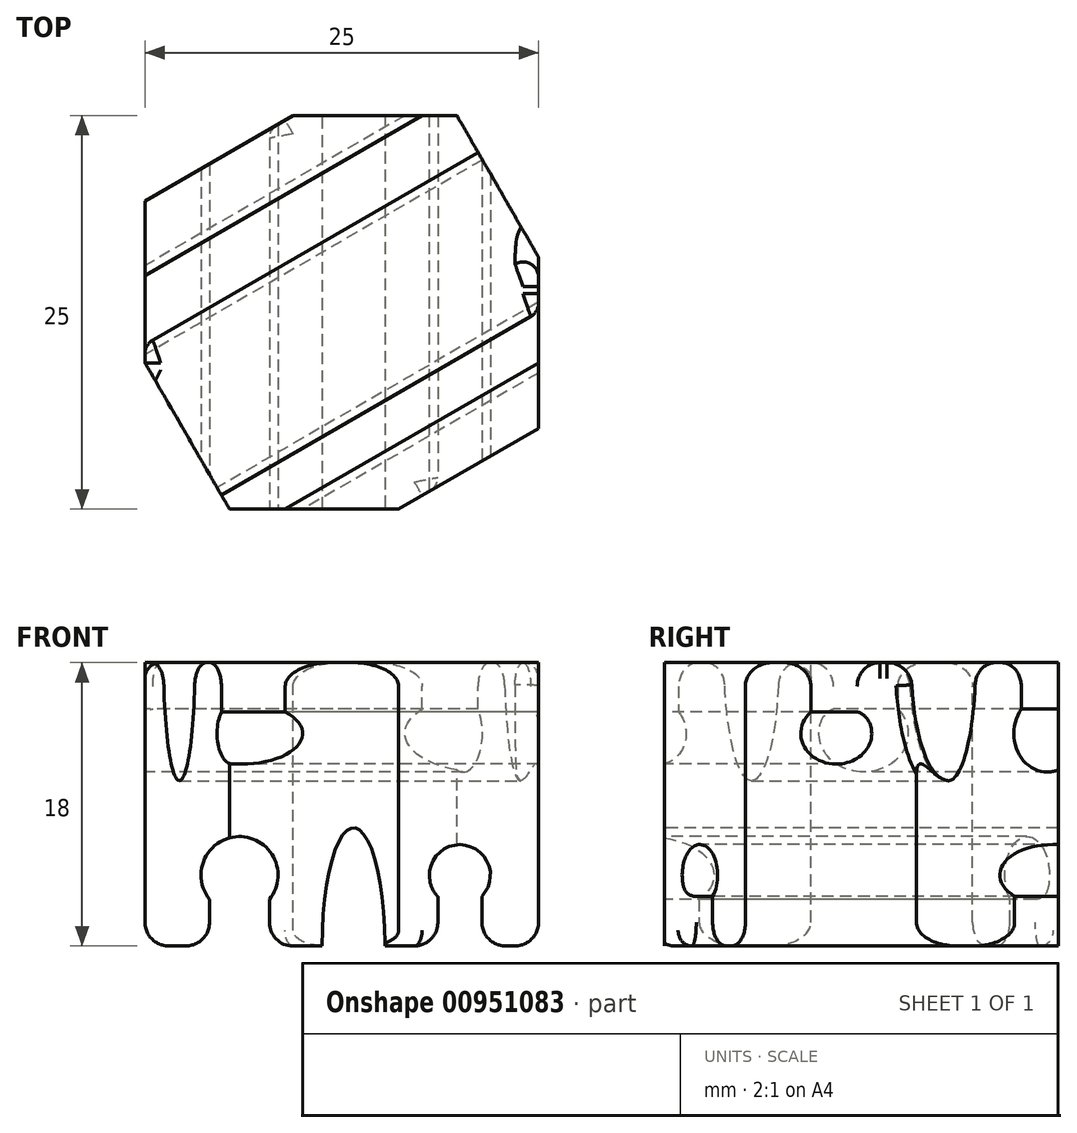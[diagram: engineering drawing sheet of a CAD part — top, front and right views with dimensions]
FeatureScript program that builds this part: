
annotation { "Feature Type Name" : "Feature", "Feature Type Description" : "" }
export const myFeature = defineFeature(function(context is Context, id is Id, definition is map)
    precondition{}
    {
        {
            var Q0;
            Q0=qCreatedBy(makeId("Top.planeOp"),FACE);
            var sketch = newSketch(context, id + "F0", { "sketchPlane" : qUnion([Q0])});
            skLineSegment(sketch, "E0.bottom", {"start": v(0, 0) * mm, "end": v(25, 0) * mm});
            skLineSegment(sketch, "E0.top", {"start": v(0, 25) * mm, "end": v(25, 25) * mm});
            skLineSegment(sketch, "E0.left", {"start": v(0, 0) * mm, "end": v(0, 25) * mm});
            skLineSegment(sketch, "E0.right", {"start": v(25, 0) * mm, "end": v(25, 25) * mm});
            skSolve(sketch);
        }
        {
            var Q0;
            Q0 = qSketchRegion(id + "F0", true);
            extrude(context, id + "F1", {"entities" : qUnion([Q0]), "depth" : 9 * mm, "offsetDistance" : 25 * mm});
        }
        {
            var Q0;
            Q0=makeQuery(id+"F1.opExtrude","SWEPT_FACE",FACE,{"disambiguationData":[OSD([sQuery(id+"F0.wireOp",EDGE,"E0.bottom")])]});
            var sketch = newSketch(context, id + "F2", { "sketchPlane" : qUnion([Q0])});
            skCircle(sketch, "E1", {"center": v(6, 4.5) * mm, "radius": 2.45 * mm});
            skPoint(sketch, "E1.centerSnap0", {"position": v(0, 4.5) * mm});
            skCircle(sketch, "E2", {"center": v(20, 4.5) * mm, "radius": 1.95 * mm});
            skEllipse(sketch, "E3", {"center": v(13.25, 0) * mm, "majorRadius": 7.5 * mm, "minorRadius": 2 * mm, "majorAxis": v(0, -1)});
            skSolve(sketch);
        }
        {
            var Q0;
            Q0 = qSketchRegion(id + "F2", true);
            var Q1;
            Q1=makeQuery(id+"F1.opExtrude","SWEPT_FACE",FACE,{"disambiguationData":[OSD([sQuery(id+"F0.wireOp",EDGE,"E0.top")])]});
            extrude(context, id + "F3", {"entities" : qUnion([Q0]), "operationType" : NewBodyOperationType.REMOVE, "endBound" : BoundingType.UP_TO_SURFACE, "oppositeDirection" : true, "depth" : 25 * mm, "endBoundEntityFace" : qUnion([Q1]), "offsetDistance" : 25 * mm});
        }
        {
            var Q0;
            Q0=makeQuery(id+"F1.opExtrude","CAP_FACE",FACE,{"disambiguationData":[OSD([sQuery(id+"F0.wireOp",EDGE,"E0.bottom"),sQuery(id+"F0.wireOp",EDGE,"E0.top"),sQuery(id+"F0.wireOp",EDGE,"E0.left"),sQuery(id+"F0.wireOp",EDGE,"E0.right")])],"isStart":false});
            var sketch = newSketch(context, id + "F4", { "sketchPlane" : qUnion([Q0])});
            skLineSegment(sketch, "E4", {"start": v(17.2, 29.5) * mm, "end": v(-4.44, 17) * mm});
            skLineSegment(sketch, "E5", {"start": v(-4.44, 17) * mm, "end": v(8.06, -4.65) * mm});
            skLineSegment(sketch, "E6", {"start": v(8.06, -4.65) * mm, "end": v(29.7, 7.85) * mm});
            skLineSegment(sketch, "E7", {"start": v(29.7, 7.85) * mm, "end": v(17.2, 29.5) * mm});
            skSolve(sketch);
        }
        {
            var Q0;
            Q0 = qSketchRegion(id + "F4", true);
            extrude(context, id + "F5", {"entities" : qUnion([Q0]), "operationType" : NewBodyOperationType.ADD, "depth" : 9 * mm, "offsetDistance" : 25 * mm});
        }
        {
            var Q0;
            Q0=makeQuery(id+"F5.opExtrude","SWEPT_FACE",FACE,{"disambiguationData":[OSD([sQuery(id+"F4.wireOp",EDGE,"E5")])]});
            var sketch = newSketch(context, id + "F6", { "sketchPlane" : qUnion([Q0])});
            skCircle(sketch, "E8", {"center": v(-10.94, 13.5) * mm, "radius": 2.45 * mm});
            skCircle(sketch, "E9", {"center": v(3.06, 13.5) * mm, "radius": 1.95 * mm});
            skEllipse(sketch, "E10", {"center": v(-3.7, 18) * mm, "majorRadius": 7.5 * mm, "minorRadius": 2 * mm, "majorAxis": v(0, -1)});
            skSolve(sketch);
        }
        {
            var Q0;
            Q0 = qSketchRegion(id + "F6", true);
            var Q1;
            Q1=makeQuery(id+"F5.opExtrude","SWEPT_FACE",FACE,{"disambiguationData":[OSD([sQuery(id+"F4.wireOp",EDGE,"E7")])]});
            extrude(context, id + "F7", {"entities" : qUnion([Q0]), "operationType" : NewBodyOperationType.REMOVE, "endBound" : BoundingType.UP_TO_SURFACE, "oppositeDirection" : true, "depth" : 25 * mm, "endBoundEntityFace" : qUnion([Q1]), "offsetDistance" : 25 * mm});
        }
        {
            var Q0;
            Q0=makeQuery(id+"F1.opExtrude","SWEPT_FACE",FACE,{"disambiguationData":[OSD([sQuery(id+"F0.wireOp",EDGE,"E0.bottom")])]});
            var sketch = newSketch(context, id + "F8", { "sketchPlane" : qUnion([Q0])});
            skLineSegment(sketch, "E11.bottom", {"start": v(4.1, 4.5) * mm, "end": v(7.9, 4.5) * mm});
            skLineSegment(sketch, "E11.top", {"start": v(4.1, -1) * mm, "end": v(7.9, -1) * mm});
            skLineSegment(sketch, "E11.left", {"start": v(4.1, 4.5) * mm, "end": v(4.1, -1) * mm});
            skLineSegment(sketch, "E11.right", {"start": v(7.9, 4.5) * mm, "end": v(7.9, -1) * mm});
            skLineSegment(sketch, "E12.bottom", {"start": v(18.6, 4.5) * mm, "end": v(21.4, 4.5) * mm});
            skLineSegment(sketch, "E12.top", {"start": v(18.6, -1) * mm, "end": v(21.4, -1) * mm});
            skLineSegment(sketch, "E12.left", {"start": v(18.6, 4.5) * mm, "end": v(18.6, -1) * mm});
            skLineSegment(sketch, "E12.right", {"start": v(21.4, 4.5) * mm, "end": v(21.4, -1) * mm});
            skSolve(sketch);
        }
        {
            var Q0;
            Q0 = qSketchRegion(id + "F8", true);
            var Q1;
            Q1=makeQuery(id+"F1.opExtrude","SWEPT_FACE",FACE,{"disambiguationData":[OSD([sQuery(id+"F0.wireOp",EDGE,"E0.top")])]});
            extrude(context, id + "F9", {"entities" : qUnion([Q0]), "operationType" : NewBodyOperationType.REMOVE, "endBound" : BoundingType.UP_TO_SURFACE, "oppositeDirection" : true, "depth" : 25 * mm, "endBoundEntityFace" : qUnion([Q1]), "offsetDistance" : 25 * mm});
        }
        {
            var Q0;
            Q0=makeQuery(id+"F5.opExtrude","SWEPT_FACE",FACE,{"disambiguationData":[OSD([sQuery(id+"F4.wireOp",EDGE,"E5")])]});
            var sketch = newSketch(context, id + "F10", { "sketchPlane" : qUnion([Q0])});
            skLineSegment(sketch, "E13.bottom", {"start": v(-12.84, 19) * mm, "end": v(-9.04, 19) * mm});
            skLineSegment(sketch, "E13.top", {"start": v(-12.84, 13.5) * mm, "end": v(-9.04, 13.5) * mm});
            skLineSegment(sketch, "E13.left", {"start": v(-12.84, 19) * mm, "end": v(-12.84, 13.5) * mm});
            skLineSegment(sketch, "E13.right", {"start": v(-9.04, 19) * mm, "end": v(-9.04, 13.5) * mm});
            skLineSegment(sketch, "E14.bottom", {"start": v(1.66, 19) * mm, "end": v(4.46, 19) * mm});
            skLineSegment(sketch, "E14.top", {"start": v(1.66, 13.5) * mm, "end": v(4.46, 13.5) * mm});
            skLineSegment(sketch, "E14.left", {"start": v(1.66, 19) * mm, "end": v(1.66, 13.5) * mm});
            skLineSegment(sketch, "E14.right", {"start": v(4.46, 19) * mm, "end": v(4.46, 13.5) * mm});
            skSolve(sketch);
        }
        {
            var Q0;
            Q0 = qSketchRegion(id + "F10", true);
            var Q1;
            Q1=makeQuery(id+"F5.opExtrude","SWEPT_FACE",FACE,{"disambiguationData":[OSD([sQuery(id+"F4.wireOp",EDGE,"E7")])]});
            extrude(context, id + "F11", {"entities" : qUnion([Q0]), "operationType" : NewBodyOperationType.REMOVE, "endBound" : BoundingType.UP_TO_SURFACE, "oppositeDirection" : true, "depth" : 25 * mm, "endBoundEntityFace" : qUnion([Q1]), "offsetDistance" : 25 * mm});
        }
        {
            var Q0;
            {var subQ0=sQuery(id+"F0.wireOp",EDGE,"E0.top");var subQ1=sQuery(id+"F4.wireOp",EDGE,"E4");var subQ2=sQuery(id+"F0.wireOp",EDGE,"E0.left");Q0=makeQuery(id+"F5.boolean.opBoolean","SPLIT",FACE,{"disambiguationData":[TD([makeQuery(id+"F5.opExtrude","SWEPT_FACE",FACE,{"disambiguationData":[OSD([subQ1])]})])],"derivedFrom":makeQuery(id+"F1.opExtrude","CAP_FACE",FACE,{"disambiguationData":[OSD([sQuery(id+"F0.wireOp",EDGE,"E0.bottom"),subQ0,subQ2,sQuery(id+"F0.wireOp",EDGE,"E0.right")])],"isStart":false})});}
            var sketch = newSketch(context, id + "F12", { "sketchPlane" : qUnion([Q0])});
            skLineSegment(sketch, "E15", {"start": v(0, 25) * mm, "end": v(9.41, 25) * mm});
            skLineSegment(sketch, "E16", {"start": v(9.41, 25) * mm, "end": v(0, 19.57) * mm});
            skLineSegment(sketch, "E17", {"start": v(0, 19.57) * mm, "end": v(0, 25) * mm});
            skSolve(sketch);
        }
        {
            var Q0;
            Q0 = qSketchRegion(id + "F12", true);
            var Q1;
            {var subQ0=sQuery(id+"F4.wireOp",EDGE,"E4");var subQ1=makeQuery(id+"F5.opExtrude","SWEPT_FACE",FACE,{"disambiguationData":[OSD([subQ0])]});var subQ2=sQuery(id+"F4.wireOp",EDGE,"E7");var subQ4=sQuery(id+"F4.wireOp",EDGE,"E5");Q1=makeQuery(id+"F11.boolean.opBoolean","SPLIT",FACE,{"disambiguationData":[TD([subQ1])],"derivedFrom":makeQuery(id+"F7.boolean.opBoolean","SPLIT",FACE,{"disambiguationData":[TD([subQ1])],"derivedFrom":makeQuery(id+"F5.opExtrude","CAP_FACE",FACE,{"disambiguationData":[OSD([subQ0,subQ4,sQuery(id+"F4.wireOp",EDGE,"E6"),subQ2])],"isStart":false})})});}
            extrude(context, id + "F13", {"entities" : qUnion([Q0]), "operationType" : NewBodyOperationType.REMOVE, "endBound" : BoundingType.UP_TO_NEXT, "oppositeDirection" : true, "depth" : 25 * mm, "endBoundEntityFace" : qUnion([Q1]), "offsetDistance" : 25 * mm});
        }
        {
            var Q0;
            {var subQ0=sQuery(id+"F0.wireOp",EDGE,"E0.bottom");var subQ1=sQuery(id+"F0.wireOp",EDGE,"E0.right");var subQ2=sQuery(id+"F4.wireOp",EDGE,"E6");Q0=makeQuery(id+"F5.boolean.opBoolean","SPLIT",FACE,{"disambiguationData":[TD([makeQuery(id+"F5.opExtrude","SWEPT_FACE",FACE,{"disambiguationData":[OSD([subQ2])]})])],"derivedFrom":makeQuery(id+"F1.opExtrude","CAP_FACE",FACE,{"disambiguationData":[OSD([subQ0,sQuery(id+"F0.wireOp",EDGE,"E0.top"),sQuery(id+"F0.wireOp",EDGE,"E0.left"),subQ1])],"isStart":false})});}
            var sketch = newSketch(context, id + "F14", { "sketchPlane" : qUnion([Q0])});
            skLineSegment(sketch, "E18", {"start": v(25, 0) * mm, "end": v(25, 5.13) * mm});
            skLineSegment(sketch, "E19", {"start": v(25, 5.13) * mm, "end": v(16.11, 0) * mm});
            skLineSegment(sketch, "E20", {"start": v(16.11, 0) * mm, "end": v(25, 0) * mm});
            skSolve(sketch);
        }
        {
            var Q0;
            Q0 = qSketchRegion(id + "F14", true);
            var Q1;
            {var subQ0=sQuery(id+"F4.wireOp",EDGE,"E5");var subQ2=sQuery(id+"F4.wireOp",EDGE,"E6");var subQ3=makeQuery(id+"F5.opExtrude","SWEPT_FACE",FACE,{"disambiguationData":[OSD([subQ2])]});var subQ4=sQuery(id+"F4.wireOp",EDGE,"E7");Q1=makeQuery(id+"F11.boolean.opBoolean","SPLIT",FACE,{"disambiguationData":[TD([subQ3])],"derivedFrom":makeQuery(id+"F7.boolean.opBoolean","SPLIT",FACE,{"disambiguationData":[TD([subQ3])],"derivedFrom":makeQuery(id+"F5.opExtrude","CAP_FACE",FACE,{"disambiguationData":[OSD([sQuery(id+"F4.wireOp",EDGE,"E4"),subQ0,subQ2,subQ4])],"isStart":false})})});}
            extrude(context, id + "F15", {"entities" : qUnion([Q0]), "operationType" : NewBodyOperationType.REMOVE, "endBound" : BoundingType.UP_TO_NEXT, "oppositeDirection" : true, "depth" : 25 * mm, "endBoundEntityFace" : qUnion([Q1]), "offsetDistance" : 25 * mm});
        }
        {
            var Q0;
            {var subQ0=sQuery(id+"F0.wireOp",EDGE,"E0.bottom");var subQ1=sQuery(id+"F4.wireOp",EDGE,"E5");var subQ2=sQuery(id+"F4.wireOp",EDGE,"E6");Q0=makeQuery(id+"F5.boolean.opBoolean","SPLIT",FACE,{"disambiguationData":[TD([makeQuery(id+"F1.opExtrude","SWEPT_FACE",FACE,{"disambiguationData":[OSD([subQ0])]})])],"derivedFrom":makeQuery(id+"F5.opExtrude","CAP_FACE",FACE,{"disambiguationData":[OSD([sQuery(id+"F4.wireOp",EDGE,"E4"),subQ1,subQ2,sQuery(id+"F4.wireOp",EDGE,"E7")])],"isStart":true})});}
            var sketch = newSketch(context, id + "F16", { "sketchPlane" : qUnion([Q0])});
            skLineSegment(sketch, "E21", {"start": v(8.06, 4.65) * mm, "end": v(5.37, 0) * mm});
            skLineSegment(sketch, "E22", {"start": v(5.37, 0) * mm, "end": v(16.11, 0) * mm});
            skLineSegment(sketch, "E23", {"start": v(16.11, 0) * mm, "end": v(8.06, 4.65) * mm});
            skSolve(sketch);
        }
        {
            var Q0;
            Q0 = qSketchRegion(id + "F16", true);
            extrude(context, id + "F17", {"entities" : qUnion([Q0]), "operationType" : NewBodyOperationType.REMOVE, "endBound" : BoundingType.UP_TO_NEXT, "oppositeDirection" : true, "depth" : 25 * mm, "offsetDistance" : 25 * mm});
        }
        {
            var Q0;
            {var subQ0=sQuery(id+"F0.wireOp",EDGE,"E0.right");var subQ1=sQuery(id+"F4.wireOp",EDGE,"E7");var subQ2=sQuery(id+"F4.wireOp",EDGE,"E6");Q0=makeQuery(id+"F5.boolean.opBoolean","SPLIT",FACE,{"disambiguationData":[TD([makeQuery(id+"F1.opExtrude","SWEPT_FACE",FACE,{"disambiguationData":[OSD([subQ0])]})])],"derivedFrom":makeQuery(id+"F5.opExtrude","CAP_FACE",FACE,{"disambiguationData":[OSD([sQuery(id+"F4.wireOp",EDGE,"E4"),sQuery(id+"F4.wireOp",EDGE,"E5"),subQ2,subQ1])],"isStart":true})});}
            var sketch = newSketch(context, id + "F18", { "sketchPlane" : qUnion([Q0])});
            skLineSegment(sketch, "E24", {"start": v(25, -5.13) * mm, "end": v(29.7, -7.85) * mm});
            skLineSegment(sketch, "E25", {"start": v(29.7, -7.85) * mm, "end": v(25, -16) * mm});
            skLineSegment(sketch, "E26", {"start": v(25, -16) * mm, "end": v(25, -5.13) * mm});
            skSolve(sketch);
        }
        {
            var Q0;
            Q0 = qSketchRegion(id + "F18", true);
            extrude(context, id + "F19", {"entities" : qUnion([Q0]), "operationType" : NewBodyOperationType.REMOVE, "endBound" : BoundingType.UP_TO_NEXT, "oppositeDirection" : true, "depth" : 25 * mm, "offsetDistance" : 25 * mm});
        }
        {
            var Q0;
            {var subQ0=sQuery(id+"F0.wireOp",EDGE,"E0.bottom");var subQ1=sQuery(id+"F4.wireOp",EDGE,"E5");var subQ2=sQuery(id+"F0.wireOp",EDGE,"E0.left");Q0=makeQuery(id+"F5.boolean.opBoolean","SPLIT",FACE,{"disambiguationData":[TD([makeQuery(id+"F5.opExtrude","SWEPT_FACE",FACE,{"disambiguationData":[OSD([subQ1])]})])],"derivedFrom":makeQuery(id+"F1.opExtrude","CAP_FACE",FACE,{"disambiguationData":[OSD([subQ0,sQuery(id+"F0.wireOp",EDGE,"E0.top"),subQ2,sQuery(id+"F0.wireOp",EDGE,"E0.right")])],"isStart":false})});}
            var sketch = newSketch(context, id + "F20", { "sketchPlane" : qUnion([Q0])});
            skLineSegment(sketch, "E27", {"start": v(0, 0) * mm, "end": v(5.37, 0) * mm});
            skLineSegment(sketch, "E28", {"start": v(5.37, 0) * mm, "end": v(0, 9.3) * mm});
            skLineSegment(sketch, "E29", {"start": v(0, 9.3) * mm, "end": v(0, 0) * mm});
            skSolve(sketch);
        }
        {
            var Q0;
            Q0 = qSketchRegion(id + "F20", true);
            extrude(context, id + "F21", {"entities" : qUnion([Q0]), "operationType" : NewBodyOperationType.REMOVE, "endBound" : BoundingType.UP_TO_NEXT, "oppositeDirection" : true, "depth" : 25 * mm, "offsetDistance" : 25 * mm});
        }
        {
            var Q0;
            {var subQ0=sQuery(id+"F0.wireOp",EDGE,"E0.top");var subQ1=sQuery(id+"F4.wireOp",EDGE,"E7");var subQ2=sQuery(id+"F0.wireOp",EDGE,"E0.right");Q0=makeQuery(id+"F5.boolean.opBoolean","SPLIT",FACE,{"disambiguationData":[TD([makeQuery(id+"F5.opExtrude","SWEPT_FACE",FACE,{"disambiguationData":[OSD([subQ1])]})])],"derivedFrom":makeQuery(id+"F1.opExtrude","CAP_FACE",FACE,{"disambiguationData":[OSD([sQuery(id+"F0.wireOp",EDGE,"E0.bottom"),subQ0,sQuery(id+"F0.wireOp",EDGE,"E0.left"),subQ2])],"isStart":false})});}
            var sketch = newSketch(context, id + "F22", { "sketchPlane" : qUnion([Q0])});
            skLineSegment(sketch, "E30", {"start": v(19.8, 25) * mm, "end": v(25, 25) * mm});
            skLineSegment(sketch, "E31", {"start": v(25, 25) * mm, "end": v(25, 16) * mm});
            skLineSegment(sketch, "E32", {"start": v(25, 16) * mm, "end": v(19.8, 25) * mm});
            skSolve(sketch);
        }
        {
            var Q0;
            Q0 = qSketchRegion(id + "F22", true);
            extrude(context, id + "F23", {"entities" : qUnion([Q0]), "operationType" : NewBodyOperationType.REMOVE, "endBound" : BoundingType.UP_TO_NEXT, "oppositeDirection" : true, "depth" : 25 * mm, "offsetDistance" : 25 * mm});
        }
        {
            var Q0;
            {var subQ0=sQuery(id+"F0.wireOp",EDGE,"E0.left");var subQ1=sQuery(id+"F4.wireOp",EDGE,"E4");var subQ2=sQuery(id+"F4.wireOp",EDGE,"E5");Q0=makeQuery(id+"F5.boolean.opBoolean","SPLIT",FACE,{"disambiguationData":[TD([makeQuery(id+"F1.opExtrude","SWEPT_FACE",FACE,{"disambiguationData":[OSD([subQ0])]})])],"derivedFrom":makeQuery(id+"F5.opExtrude","CAP_FACE",FACE,{"disambiguationData":[OSD([subQ1,subQ2,sQuery(id+"F4.wireOp",EDGE,"E6"),sQuery(id+"F4.wireOp",EDGE,"E7")])],"isStart":true})});}
            var sketch = newSketch(context, id + "F24", { "sketchPlane" : qUnion([Q0])});
            skLineSegment(sketch, "E33", {"start": v(-4.44, -17) * mm, "end": v(0, -19.57) * mm});
            skLineSegment(sketch, "E34", {"start": v(0, -19.57) * mm, "end": v(0, -9.3) * mm});
            skLineSegment(sketch, "E35", {"start": v(0, -9.3) * mm, "end": v(-4.44, -17) * mm});
            skSolve(sketch);
        }
        {
            var Q0;
            Q0 = qSketchRegion(id + "F24", true);
            extrude(context, id + "F25", {"entities" : qUnion([Q0]), "operationType" : NewBodyOperationType.REMOVE, "endBound" : BoundingType.UP_TO_NEXT, "oppositeDirection" : true, "depth" : 25 * mm, "offsetDistance" : 25 * mm});
        }
        {
            var Q0;
            {var subQ0=sQuery(id+"F0.wireOp",EDGE,"E0.top");var subQ1=sQuery(id+"F4.wireOp",EDGE,"E4");var subQ2=sQuery(id+"F4.wireOp",EDGE,"E7");Q0=makeQuery(id+"F5.boolean.opBoolean","SPLIT",FACE,{"disambiguationData":[TD([makeQuery(id+"F1.opExtrude","SWEPT_FACE",FACE,{"disambiguationData":[OSD([subQ0])]})])],"derivedFrom":makeQuery(id+"F5.opExtrude","CAP_FACE",FACE,{"disambiguationData":[OSD([subQ1,sQuery(id+"F4.wireOp",EDGE,"E5"),sQuery(id+"F4.wireOp",EDGE,"E6"),subQ2])],"isStart":true})});}
            var sketch = newSketch(context, id + "F26", { "sketchPlane" : qUnion([Q0])});
            skLineSegment(sketch, "E36", {"start": v(17.2, -29.5) * mm, "end": v(9.41, -25) * mm});
            skLineSegment(sketch, "E37", {"start": v(9.41, -25) * mm, "end": v(19.8, -25) * mm});
            skLineSegment(sketch, "E38", {"start": v(19.8, -25) * mm, "end": v(17.2, -29.5) * mm});
            skSolve(sketch);
        }
        {
            var Q0;
            Q0 = qSketchRegion(id + "F26", true);
            extrude(context, id + "F27", {"entities" : qUnion([Q0]), "operationType" : NewBodyOperationType.REMOVE, "endBound" : BoundingType.UP_TO_NEXT, "oppositeDirection" : true, "depth" : 25 * mm, "offsetDistance" : 25 * mm});
        }
        {
            var Q0;
            Q0=makeQuery(id+"F5.opExtrude","CAP_EDGE",EDGE,{"disambiguationData":[OSD([sQuery(id+"F4.wireOp",EDGE,"E6")])],"isStart":false});
            var Q1;
            Q1=makeQuery(id+"F7.boolean.opBoolean","COPY",EDGE,{"derivedFrom":makeQuery(id+"F7.opExtrude","CAP_EDGE",EDGE,{"disambiguationData":[OSD([sQuery(id+"F6.wireOp",EDGE,"nKPkvaN6-t2cK-g7Lz-JJJY-Wnfh6WaRCjng")]),topologyDisambiguationEdgeConnected([makeQuery(id+"F5.opExtrude","CAP_FACE",FACE,{"disambiguationData":[OSD([sQuery(id+"F4.wireOp",EDGE,"E4"),sQuery(id+"F4.wireOp",EDGE,"E5"),sQuery(id+"F4.wireOp",EDGE,"E6"),sQuery(id+"F4.wireOp",EDGE,"E7")])],"isStart":false})]),OD(1.0)],"isStart":false})});
            var Q2;
            {var subQ0=sQuery(id+"F4.wireOp",EDGE,"E5");var subQ1=sQuery(id+"F4.wireOp",EDGE,"E6");var subQ2=sQuery(id+"F4.wireOp",EDGE,"E7");Q2=makeQuery(id+"F11.boolean.opBoolean","INTERSECT",EDGE,{"derivedFrom":[makeQuery(id+"F7.boolean.opBoolean","SPLIT",FACE,{"disambiguationData":[TD([makeQuery(id+"F5.opExtrude","SWEPT_FACE",FACE,{"disambiguationData":[OSD([subQ1])]})])],"derivedFrom":makeQuery(id+"F5.opExtrude","CAP_FACE",FACE,{"disambiguationData":[OSD([sQuery(id+"F4.wireOp",EDGE,"E4"),subQ0,subQ1,subQ2])],"isStart":false})}),makeQuery(id+"F11.opExtrude","SWEPT_FACE",FACE,{"disambiguationData":[OSD([sQuery(id+"F10.wireOp",EDGE,"E14.left")])]})]});}
            var Q3;
            {var subQ0=sQuery(id+"F4.wireOp",EDGE,"E5");var subQ1=sQuery(id+"F4.wireOp",EDGE,"E6");var subQ2=sQuery(id+"F4.wireOp",EDGE,"E7");Q3=makeQuery(id+"F11.boolean.opBoolean","INTERSECT",EDGE,{"derivedFrom":[makeQuery(id+"F7.boolean.opBoolean","SPLIT",FACE,{"disambiguationData":[TD([makeQuery(id+"F5.opExtrude","SWEPT_FACE",FACE,{"disambiguationData":[OSD([subQ1])]})])],"derivedFrom":makeQuery(id+"F5.opExtrude","CAP_FACE",FACE,{"disambiguationData":[OSD([sQuery(id+"F4.wireOp",EDGE,"E4"),subQ0,subQ1,subQ2])],"isStart":false})}),makeQuery(id+"F11.opExtrude","SWEPT_FACE",FACE,{"disambiguationData":[OSD([sQuery(id+"F10.wireOp",EDGE,"E14.right")])]})]});}
            var Q4;
            Q4=makeQuery(id+"F7.boolean.opBoolean","COPY",EDGE,{"derivedFrom":makeQuery(id+"F7.opExtrude","CAP_EDGE",EDGE,{"disambiguationData":[OSD([sQuery(id+"F6.wireOp",EDGE,"nKPkvaN6-t2cK-g7Lz-JJJY-Wnfh6WaRCjng")]),topologyDisambiguationEdgeConnected([makeQuery(id+"F5.opExtrude","CAP_FACE",FACE,{"disambiguationData":[OSD([sQuery(id+"F4.wireOp",EDGE,"E4"),sQuery(id+"F4.wireOp",EDGE,"E5"),sQuery(id+"F4.wireOp",EDGE,"E6"),sQuery(id+"F4.wireOp",EDGE,"E7")])],"isStart":false})]),OD(0.0)],"isStart":false})});
            var Q5;
            {var subQ0=sQuery(id+"F4.wireOp",EDGE,"E4");var subQ1=sQuery(id+"F4.wireOp",EDGE,"E7");var subQ2=sQuery(id+"F4.wireOp",EDGE,"E5");Q5=makeQuery(id+"F11.boolean.opBoolean","INTERSECT",EDGE,{"derivedFrom":[makeQuery(id+"F7.boolean.opBoolean","SPLIT",FACE,{"disambiguationData":[TD([makeQuery(id+"F5.opExtrude","SWEPT_FACE",FACE,{"disambiguationData":[OSD([subQ0])]})])],"derivedFrom":makeQuery(id+"F5.opExtrude","CAP_FACE",FACE,{"disambiguationData":[OSD([subQ0,subQ2,sQuery(id+"F4.wireOp",EDGE,"E6"),subQ1])],"isStart":false})}),makeQuery(id+"F11.opExtrude","SWEPT_FACE",FACE,{"disambiguationData":[OSD([sQuery(id+"F10.wireOp",EDGE,"E13.right")])]})]});}
            var Q6;
            {var subQ0=sQuery(id+"F4.wireOp",EDGE,"E4");var subQ1=sQuery(id+"F4.wireOp",EDGE,"E7");var subQ2=sQuery(id+"F4.wireOp",EDGE,"E5");Q6=makeQuery(id+"F11.boolean.opBoolean","INTERSECT",EDGE,{"derivedFrom":[makeQuery(id+"F7.boolean.opBoolean","SPLIT",FACE,{"disambiguationData":[TD([makeQuery(id+"F5.opExtrude","SWEPT_FACE",FACE,{"disambiguationData":[OSD([subQ0])]})])],"derivedFrom":makeQuery(id+"F5.opExtrude","CAP_FACE",FACE,{"disambiguationData":[OSD([subQ0,subQ2,sQuery(id+"F4.wireOp",EDGE,"E6"),subQ1])],"isStart":false})}),makeQuery(id+"F11.opExtrude","SWEPT_FACE",FACE,{"disambiguationData":[OSD([sQuery(id+"F10.wireOp",EDGE,"E13.left")])]})]});}
            var Q7;
            Q7=makeQuery(id+"F5.opExtrude","CAP_EDGE",EDGE,{"disambiguationData":[OSD([sQuery(id+"F4.wireOp",EDGE,"E4")])],"isStart":false});
            var Q8;
            Q8=makeQuery(id+"F1.opExtrude","CAP_EDGE",EDGE,{"disambiguationData":[OSD([sQuery(id+"F0.wireOp",EDGE,"E0.left")])],"isStart":true});
            var Q9;
            {var subQ0=sQuery(id+"F0.wireOp",EDGE,"E0.bottom");var subQ1=sQuery(id+"F0.wireOp",EDGE,"E0.top");var subQ2=sQuery(id+"F0.wireOp",EDGE,"E0.left");Q9=makeQuery(id+"F9.boolean.opBoolean","INTERSECT",EDGE,{"derivedFrom":[makeQuery(id+"F3.boolean.opBoolean","SPLIT",FACE,{"disambiguationData":[TD([makeQuery(id+"F1.opExtrude","SWEPT_FACE",FACE,{"disambiguationData":[OSD([subQ2])]})])],"derivedFrom":makeQuery(id+"F1.opExtrude","CAP_FACE",FACE,{"disambiguationData":[OSD([subQ0,subQ1,subQ2,sQuery(id+"F0.wireOp",EDGE,"E0.right")])],"isStart":true})}),makeQuery(id+"F9.opExtrude","SWEPT_FACE",FACE,{"disambiguationData":[OSD([sQuery(id+"F8.wireOp",EDGE,"E11.left")])]})]});}
            var Q10;
            {var subQ0=sQuery(id+"F0.wireOp",EDGE,"E0.bottom");var subQ1=sQuery(id+"F0.wireOp",EDGE,"E0.top");var subQ2=sQuery(id+"F0.wireOp",EDGE,"E0.left");Q10=makeQuery(id+"F9.boolean.opBoolean","INTERSECT",EDGE,{"derivedFrom":[makeQuery(id+"F3.boolean.opBoolean","SPLIT",FACE,{"disambiguationData":[TD([makeQuery(id+"F1.opExtrude","SWEPT_FACE",FACE,{"disambiguationData":[OSD([subQ2])]})])],"derivedFrom":makeQuery(id+"F1.opExtrude","CAP_FACE",FACE,{"disambiguationData":[OSD([subQ0,subQ1,subQ2,sQuery(id+"F0.wireOp",EDGE,"E0.right")])],"isStart":true})}),makeQuery(id+"F9.opExtrude","SWEPT_FACE",FACE,{"disambiguationData":[OSD([sQuery(id+"F8.wireOp",EDGE,"E11.right")])]})]});}
            var Q11;
            Q11=makeQuery(id+"F3.boolean.opBoolean","INTERSECT",EDGE,{"disambiguationData":[OD(0.0)],"derivedFrom":[makeQuery(id+"F1.opExtrude","CAP_FACE",FACE,{"disambiguationData":[OSD([sQuery(id+"F0.wireOp",EDGE,"E0.bottom"),sQuery(id+"F0.wireOp",EDGE,"E0.top"),sQuery(id+"F0.wireOp",EDGE,"E0.left"),sQuery(id+"F0.wireOp",EDGE,"E0.right")])],"isStart":true}),makeQuery(id+"F3.opExtrude","SWEPT_FACE",FACE,{"disambiguationData":[OSD([sQuery(id+"F2.wireOp",EDGE,"Dy1kn0kp-zmKv-evS4-W5LW-9Hcu3yojOo55")])]})]});
            var Q12;
            Q12=makeQuery(id+"F3.boolean.opBoolean","INTERSECT",EDGE,{"disambiguationData":[OD(1.0)],"derivedFrom":[makeQuery(id+"F1.opExtrude","CAP_FACE",FACE,{"disambiguationData":[OSD([sQuery(id+"F0.wireOp",EDGE,"E0.bottom"),sQuery(id+"F0.wireOp",EDGE,"E0.top"),sQuery(id+"F0.wireOp",EDGE,"E0.left"),sQuery(id+"F0.wireOp",EDGE,"E0.right")])],"isStart":true}),makeQuery(id+"F3.opExtrude","SWEPT_FACE",FACE,{"disambiguationData":[OSD([sQuery(id+"F2.wireOp",EDGE,"Dy1kn0kp-zmKv-evS4-W5LW-9Hcu3yojOo55")])]})]});
            var Q13;
            {var subQ0=sQuery(id+"F0.wireOp",EDGE,"E0.bottom");var subQ1=sQuery(id+"F0.wireOp",EDGE,"E0.right");var subQ2=sQuery(id+"F0.wireOp",EDGE,"E0.top");Q13=makeQuery(id+"F9.boolean.opBoolean","INTERSECT",EDGE,{"derivedFrom":[makeQuery(id+"F3.boolean.opBoolean","SPLIT",FACE,{"disambiguationData":[TD([makeQuery(id+"F1.opExtrude","SWEPT_FACE",FACE,{"disambiguationData":[OSD([subQ1])]})])],"derivedFrom":makeQuery(id+"F1.opExtrude","CAP_FACE",FACE,{"disambiguationData":[OSD([subQ0,subQ2,sQuery(id+"F0.wireOp",EDGE,"E0.left"),subQ1])],"isStart":true})}),makeQuery(id+"F9.opExtrude","SWEPT_FACE",FACE,{"disambiguationData":[OSD([sQuery(id+"F8.wireOp",EDGE,"E12.left")])]})]});}
            var Q14;
            {var subQ0=sQuery(id+"F0.wireOp",EDGE,"E0.bottom");var subQ1=sQuery(id+"F0.wireOp",EDGE,"E0.right");var subQ2=sQuery(id+"F0.wireOp",EDGE,"E0.top");Q14=makeQuery(id+"F9.boolean.opBoolean","INTERSECT",EDGE,{"derivedFrom":[makeQuery(id+"F3.boolean.opBoolean","SPLIT",FACE,{"disambiguationData":[TD([makeQuery(id+"F1.opExtrude","SWEPT_FACE",FACE,{"disambiguationData":[OSD([subQ1])]})])],"derivedFrom":makeQuery(id+"F1.opExtrude","CAP_FACE",FACE,{"disambiguationData":[OSD([subQ0,subQ2,sQuery(id+"F0.wireOp",EDGE,"E0.left"),subQ1])],"isStart":true})}),makeQuery(id+"F9.opExtrude","SWEPT_FACE",FACE,{"disambiguationData":[OSD([sQuery(id+"F8.wireOp",EDGE,"E12.right")])]})]});}
            var Q15;
            Q15=makeQuery(id+"F1.opExtrude","CAP_EDGE",EDGE,{"disambiguationData":[OSD([sQuery(id+"F0.wireOp",EDGE,"E0.right")])],"isStart":true});
            var Q16;
            Q16=makeQuery(id+"F7.boolean.opBoolean","INTERSECT",EDGE,{"disambiguationData":[OD(1.0)],"derivedFrom":[makeQuery(id+"F5.opExtrude","CAP_FACE",FACE,{"disambiguationData":[OSD([sQuery(id+"F4.wireOp",EDGE,"E4"),sQuery(id+"F4.wireOp",EDGE,"E5"),sQuery(id+"F4.wireOp",EDGE,"E6"),sQuery(id+"F4.wireOp",EDGE,"E7")])],"isStart":false}),makeQuery(id+"F7.opExtrude","SWEPT_FACE",FACE,{"disambiguationData":[OSD([sQuery(id+"F6.wireOp",EDGE,"E10")])]})]});
            var Q17;
            Q17=makeQuery(id+"F7.boolean.opBoolean","INTERSECT",EDGE,{"disambiguationData":[OD(0.0)],"derivedFrom":[makeQuery(id+"F5.opExtrude","CAP_FACE",FACE,{"disambiguationData":[OSD([sQuery(id+"F4.wireOp",EDGE,"E4"),sQuery(id+"F4.wireOp",EDGE,"E5"),sQuery(id+"F4.wireOp",EDGE,"E6"),sQuery(id+"F4.wireOp",EDGE,"E7")])],"isStart":false}),makeQuery(id+"F7.opExtrude","SWEPT_FACE",FACE,{"disambiguationData":[OSD([sQuery(id+"F6.wireOp",EDGE,"E10")])]})]});
            fillet(context, id + "F28", {"entities" : qUnion([Q0, Q1, Q2, Q3, Q4, Q5, Q6, Q7, Q8, Q9, Q10, Q11, Q12, Q13, Q14, Q15, Q16, Q17]), "radius" : 1.5 * mm, "tangentPropagation" : true, "allowEdgeOverflow" : false});
        }
        {
            var Q0;
            Q0=makeQuery(id+"F15.boolean.opBoolean","COPY",EDGE,{"derivedFrom":makeQuery(id+"F15.opExtrude","CAP_EDGE",EDGE,{"disambiguationData":[OSD([sQuery(id+"F14.wireOp",EDGE,"E19")]),topologyDisambiguationEdgeConnected([makeQuery(id+"F3.boolean.opBoolean","COPY",FACE,{"derivedFrom":makeQuery(id+"F3.opExtrude","SWEPT_FACE",FACE,{"disambiguationData":[OSD([sQuery(id+"F2.wireOp",EDGE,"E2")])]})})])],"isStart":false})});
            var Q1;
            Q1=makeQuery(id+"F3.boolean.opBoolean","COPY",EDGE,{"derivedFrom":makeQuery(id+"F3.opExtrude","CAP_EDGE",EDGE,{"disambiguationData":[OSD([sQuery(id+"F2.wireOp",EDGE,"E1")])],"isStart":true})});
            var Q2;
            Q2=makeQuery(id+"F21.boolean.opBoolean","COPY",EDGE,{"derivedFrom":makeQuery(id+"F21.opExtrude","CAP_EDGE",EDGE,{"disambiguationData":[OSD([sQuery(id+"F20.wireOp",EDGE,"E28")]),topologyDisambiguationEdgeConnected([makeQuery(id+"F3.boolean.opBoolean","COPY",FACE,{"derivedFrom":makeQuery(id+"F3.opExtrude","SWEPT_FACE",FACE,{"disambiguationData":[OSD([sQuery(id+"F2.wireOp",EDGE,"E1")])]})})])],"isStart":false})});
            var Q3;
            Q3=makeQuery(id+"F17.boolean.opBoolean","COPY",EDGE,{"derivedFrom":makeQuery(id+"F17.opExtrude","CAP_EDGE",EDGE,{"disambiguationData":[OSD([sQuery(id+"F16.wireOp",EDGE,"E22")]),topologyDisambiguationEdgeConnected([makeQuery(id+"F7.boolean.opBoolean","COPY",FACE,{"derivedFrom":makeQuery(id+"F7.opExtrude","SWEPT_FACE",FACE,{"disambiguationData":[OSD([sQuery(id+"F6.wireOp",EDGE,"E9")])]})})])],"isStart":false})});
            var Q4;
            Q4=makeQuery(id+"F7.boolean.opBoolean","COPY",EDGE,{"derivedFrom":makeQuery(id+"F7.opExtrude","CAP_EDGE",EDGE,{"disambiguationData":[OSD([sQuery(id+"F6.wireOp",EDGE,"E9")])],"isStart":true})});
            var Q5;
            Q5=makeQuery(id+"F25.boolean.opBoolean","COPY",EDGE,{"derivedFrom":makeQuery(id+"F25.opExtrude","CAP_EDGE",EDGE,{"disambiguationData":[OSD([sQuery(id+"F24.wireOp",EDGE,"E34")]),topologyDisambiguationEdgeConnected([makeQuery(id+"F7.boolean.opBoolean","COPY",FACE,{"derivedFrom":makeQuery(id+"F7.opExtrude","SWEPT_FACE",FACE,{"disambiguationData":[OSD([sQuery(id+"F6.wireOp",EDGE,"E8")])]})})])],"isStart":false})});
            var Q6;
            Q6=makeQuery(id+"F19.boolean.opBoolean","COPY",EDGE,{"derivedFrom":makeQuery(id+"F19.opExtrude","CAP_EDGE",EDGE,{"disambiguationData":[OSD([sQuery(id+"F18.wireOp",EDGE,"E26")]),topologyDisambiguationEdgeConnected([makeQuery(id+"F7.boolean.opBoolean","COPY",FACE,{"derivedFrom":makeQuery(id+"F7.opExtrude","SWEPT_FACE",FACE,{"disambiguationData":[OSD([sQuery(id+"F6.wireOp",EDGE,"E9")])]})})])],"isStart":false})});
            var Q7;
            Q7=makeQuery(id+"F7.boolean.opBoolean","COPY",EDGE,{"derivedFrom":makeQuery(id+"F7.opExtrude","CAP_EDGE",EDGE,{"disambiguationData":[OSD([sQuery(id+"F6.wireOp",EDGE,"E8")])],"isStart":false})});
            var Q8;
            Q8=makeQuery(id+"F27.boolean.opBoolean","COPY",EDGE,{"derivedFrom":makeQuery(id+"F27.opExtrude","CAP_EDGE",EDGE,{"disambiguationData":[OSD([sQuery(id+"F26.wireOp",EDGE,"E37")]),topologyDisambiguationEdgeConnected([makeQuery(id+"F7.boolean.opBoolean","COPY",FACE,{"derivedFrom":makeQuery(id+"F7.opExtrude","SWEPT_FACE",FACE,{"disambiguationData":[OSD([sQuery(id+"F6.wireOp",EDGE,"E8")])]})})])],"isStart":false})});
            var Q9;
            Q9=makeQuery(id+"F23.boolean.opBoolean","COPY",EDGE,{"derivedFrom":makeQuery(id+"F23.opExtrude","CAP_EDGE",EDGE,{"disambiguationData":[OSD([sQuery(id+"F22.wireOp",EDGE,"E32")]),topologyDisambiguationEdgeConnected([makeQuery(id+"F3.boolean.opBoolean","COPY",FACE,{"derivedFrom":makeQuery(id+"F3.opExtrude","SWEPT_FACE",FACE,{"disambiguationData":[OSD([sQuery(id+"F2.wireOp",EDGE,"E2")])]})})])],"isStart":false})});
            var Q10;
            Q10=makeQuery(id+"F3.boolean.opBoolean","COPY",EDGE,{"derivedFrom":makeQuery(id+"F3.opExtrude","CAP_EDGE",EDGE,{"disambiguationData":[OSD([sQuery(id+"F2.wireOp",EDGE,"E2")])],"isStart":false})});
            var Q11;
            Q11=makeQuery(id+"F13.boolean.opBoolean","COPY",EDGE,{"derivedFrom":makeQuery(id+"F13.opExtrude","CAP_EDGE",EDGE,{"disambiguationData":[OSD([sQuery(id+"F12.wireOp",EDGE,"E16")]),topologyDisambiguationEdgeConnected([makeQuery(id+"F3.boolean.opBoolean","COPY",FACE,{"derivedFrom":makeQuery(id+"F3.opExtrude","SWEPT_FACE",FACE,{"disambiguationData":[OSD([sQuery(id+"F2.wireOp",EDGE,"E1")])]})})])],"isStart":false})});
            var Q12;
            Q12=makeQuery(id+"F7.boolean.opBoolean","COPY",EDGE,{"derivedFrom":makeQuery(id+"F7.opExtrude","CAP_EDGE",EDGE,{"disambiguationData":[OSD([sQuery(id+"F6.wireOp",EDGE,"E10")])],"isStart":true})});
            var Q13;
            Q13=makeQuery(id+"F3.boolean.opBoolean","COPY",EDGE,{"derivedFrom":makeQuery(id+"F3.opExtrude","CAP_EDGE",EDGE,{"disambiguationData":[OSD([sQuery(id+"F2.wireOp",EDGE,"E3")])],"isStart":true})});
            var Q14;
            Q14=makeQuery(id+"F7.boolean.opBoolean","COPY",EDGE,{"derivedFrom":makeQuery(id+"F7.opExtrude","CAP_EDGE",EDGE,{"disambiguationData":[OSD([sQuery(id+"F6.wireOp",EDGE,"E10")])],"isStart":false})});
            var Q15;
            Q15=makeQuery(id+"F3.boolean.opBoolean","COPY",EDGE,{"derivedFrom":makeQuery(id+"F3.opExtrude","CAP_EDGE",EDGE,{"disambiguationData":[OSD([sQuery(id+"F2.wireOp",EDGE,"E3")])],"isStart":false})});
            var Q16;
            {var subQ0=sQuery(id+"F0.wireOp",EDGE,"E0.bottom");var subQ1=sQuery(id+"F0.wireOp",EDGE,"E0.top");var subQ2=sQuery(id+"F0.wireOp",EDGE,"E0.left");Q16=makeQuery(id+"F28.opFillet","BLEND_EDGE",EDGE,{"blendedFrom":[makeQuery(id+"F9.boolean.opBoolean","INTERSECT",EDGE,{"derivedFrom":[makeQuery(id+"F3.boolean.opBoolean","SPLIT",FACE,{"disambiguationData":[TD([makeQuery(id+"F1.opExtrude","SWEPT_FACE",FACE,{"disambiguationData":[OSD([subQ2])]})])],"derivedFrom":makeQuery(id+"F1.opExtrude","CAP_FACE",FACE,{"disambiguationData":[OSD([subQ0,subQ1,subQ2,sQuery(id+"F0.wireOp",EDGE,"E0.right")])],"isStart":true})}),makeQuery(id+"F9.opExtrude","SWEPT_FACE",FACE,{"disambiguationData":[OSD([sQuery(id+"F8.wireOp",EDGE,"E11.right")])]})]}),makeQuery(id+"F13.boolean.opBoolean","MERGE",FACE,{"derivedFrom":[makeQuery(id+"F5.opExtrude","SWEPT_FACE",FACE,{"disambiguationData":[OSD([sQuery(id+"F4.wireOp",EDGE,"E4")])]})],"fromTools":[makeQuery(id+"F13.opExtrude","SWEPT_FACE",FACE,{"disambiguationData":[OSD([sQuery(id+"F12.wireOp",EDGE,"E16")])]})]})],"blendedInto":[makeQuery(id+"F13.boolean.opBoolean","MERGE",FACE,{"derivedFrom":[makeQuery(id+"F5.opExtrude","SWEPT_FACE",FACE,{"disambiguationData":[OSD([sQuery(id+"F4.wireOp",EDGE,"E4")])]})],"fromTools":[makeQuery(id+"F13.opExtrude","SWEPT_FACE",FACE,{"disambiguationData":[OSD([sQuery(id+"F12.wireOp",EDGE,"E16")])]})]})]});}
            var Q17;
            Q17=makeQuery(id+"F28.opFillet","BLEND_EDGE",EDGE,{"blendedFrom":[makeQuery(id+"F7.boolean.opBoolean","INTERSECT",EDGE,{"disambiguationData":[OD(1.0)],"derivedFrom":[makeQuery(id+"F5.opExtrude","CAP_FACE",FACE,{"disambiguationData":[OSD([sQuery(id+"F4.wireOp",EDGE,"E4"),sQuery(id+"F4.wireOp",EDGE,"E5"),sQuery(id+"F4.wireOp",EDGE,"E6"),sQuery(id+"F4.wireOp",EDGE,"E7")])],"isStart":false}),makeQuery(id+"F7.opExtrude","SWEPT_FACE",FACE,{"disambiguationData":[OSD([sQuery(id+"F6.wireOp",EDGE,"E10")])]})]}),makeQuery(id+"F19.boolean.opBoolean","MERGE",FACE,{"derivedFrom":[makeQuery(id+"F1.opExtrude","SWEPT_FACE",FACE,{"disambiguationData":[OSD([sQuery(id+"F0.wireOp",EDGE,"E0.right")])]})],"fromTools":[makeQuery(id+"F19.opExtrude","SWEPT_FACE",FACE,{"disambiguationData":[OSD([sQuery(id+"F18.wireOp",EDGE,"E26")])]})]})],"blendedInto":[makeQuery(id+"F19.boolean.opBoolean","MERGE",FACE,{"derivedFrom":[makeQuery(id+"F1.opExtrude","SWEPT_FACE",FACE,{"disambiguationData":[OSD([sQuery(id+"F0.wireOp",EDGE,"E0.right")])]})],"fromTools":[makeQuery(id+"F19.opExtrude","SWEPT_FACE",FACE,{"disambiguationData":[OSD([sQuery(id+"F18.wireOp",EDGE,"E26")])]})]})]});
            var Q18;
            {var subQ0=sQuery(id+"F4.wireOp",EDGE,"E4");var subQ1=sQuery(id+"F4.wireOp",EDGE,"E7");var subQ2=sQuery(id+"F4.wireOp",EDGE,"E5");Q18=makeQuery(id+"F28.opFillet","BLEND_EDGE",EDGE,{"blendedFrom":[makeQuery(id+"F11.boolean.opBoolean","INTERSECT",EDGE,{"derivedFrom":[makeQuery(id+"F7.boolean.opBoolean","SPLIT",FACE,{"disambiguationData":[TD([makeQuery(id+"F5.opExtrude","SWEPT_FACE",FACE,{"disambiguationData":[OSD([subQ0])]})])],"derivedFrom":makeQuery(id+"F5.opExtrude","CAP_FACE",FACE,{"disambiguationData":[OSD([subQ0,subQ2,sQuery(id+"F4.wireOp",EDGE,"E6"),subQ1])],"isStart":false})}),makeQuery(id+"F11.opExtrude","SWEPT_FACE",FACE,{"disambiguationData":[OSD([sQuery(id+"F10.wireOp",EDGE,"E13.right")])]})]}),makeQuery(id+"F25.boolean.opBoolean","MERGE",FACE,{"derivedFrom":[makeQuery(id+"F1.opExtrude","SWEPT_FACE",FACE,{"disambiguationData":[OSD([sQuery(id+"F0.wireOp",EDGE,"E0.left")])]})],"fromTools":[makeQuery(id+"F25.opExtrude","SWEPT_FACE",FACE,{"disambiguationData":[OSD([sQuery(id+"F24.wireOp",EDGE,"E34")])]})]})],"blendedInto":[makeQuery(id+"F25.boolean.opBoolean","MERGE",FACE,{"derivedFrom":[makeQuery(id+"F1.opExtrude","SWEPT_FACE",FACE,{"disambiguationData":[OSD([sQuery(id+"F0.wireOp",EDGE,"E0.left")])]})],"fromTools":[makeQuery(id+"F25.opExtrude","SWEPT_FACE",FACE,{"disambiguationData":[OSD([sQuery(id+"F24.wireOp",EDGE,"E34")])]})]})]});}
            var Q19;
            {var subQ0=sQuery(id+"F0.wireOp",EDGE,"E0.bottom");var subQ1=sQuery(id+"F0.wireOp",EDGE,"E0.right");var subQ2=sQuery(id+"F0.wireOp",EDGE,"E0.top");Q19=makeQuery(id+"F28.opFillet","BLEND_EDGE",EDGE,{"blendedFrom":[makeQuery(id+"F9.boolean.opBoolean","INTERSECT",EDGE,{"derivedFrom":[makeQuery(id+"F3.boolean.opBoolean","SPLIT",FACE,{"disambiguationData":[TD([makeQuery(id+"F1.opExtrude","SWEPT_FACE",FACE,{"disambiguationData":[OSD([subQ1])]})])],"derivedFrom":makeQuery(id+"F1.opExtrude","CAP_FACE",FACE,{"disambiguationData":[OSD([subQ0,subQ2,sQuery(id+"F0.wireOp",EDGE,"E0.left"),subQ1])],"isStart":true})}),makeQuery(id+"F9.opExtrude","SWEPT_FACE",FACE,{"disambiguationData":[OSD([sQuery(id+"F8.wireOp",EDGE,"E12.left")])]})]}),makeQuery(id+"F15.boolean.opBoolean","MERGE",FACE,{"derivedFrom":[makeQuery(id+"F5.opExtrude","SWEPT_FACE",FACE,{"disambiguationData":[OSD([sQuery(id+"F4.wireOp",EDGE,"E6")])]})],"fromTools":[makeQuery(id+"F15.opExtrude","SWEPT_FACE",FACE,{"disambiguationData":[OSD([sQuery(id+"F14.wireOp",EDGE,"E19")])]})]})],"blendedInto":[makeQuery(id+"F15.boolean.opBoolean","MERGE",FACE,{"derivedFrom":[makeQuery(id+"F5.opExtrude","SWEPT_FACE",FACE,{"disambiguationData":[OSD([sQuery(id+"F4.wireOp",EDGE,"E6")])]})],"fromTools":[makeQuery(id+"F15.opExtrude","SWEPT_FACE",FACE,{"disambiguationData":[OSD([sQuery(id+"F14.wireOp",EDGE,"E19")])]})]})]});}
            fillet(context, id + "F29", {"entities" : qUnion([Q0, Q1, Q2, Q3, Q4, Q5, Q6, Q7, Q8, Q9, Q10, Q11, Q12, Q13, Q14, Q15, Q16, Q17, Q18, Q19]), "radius" : 1 * mm, "tangentPropagation" : true, "allowEdgeOverflow" : false});
        }
    });
